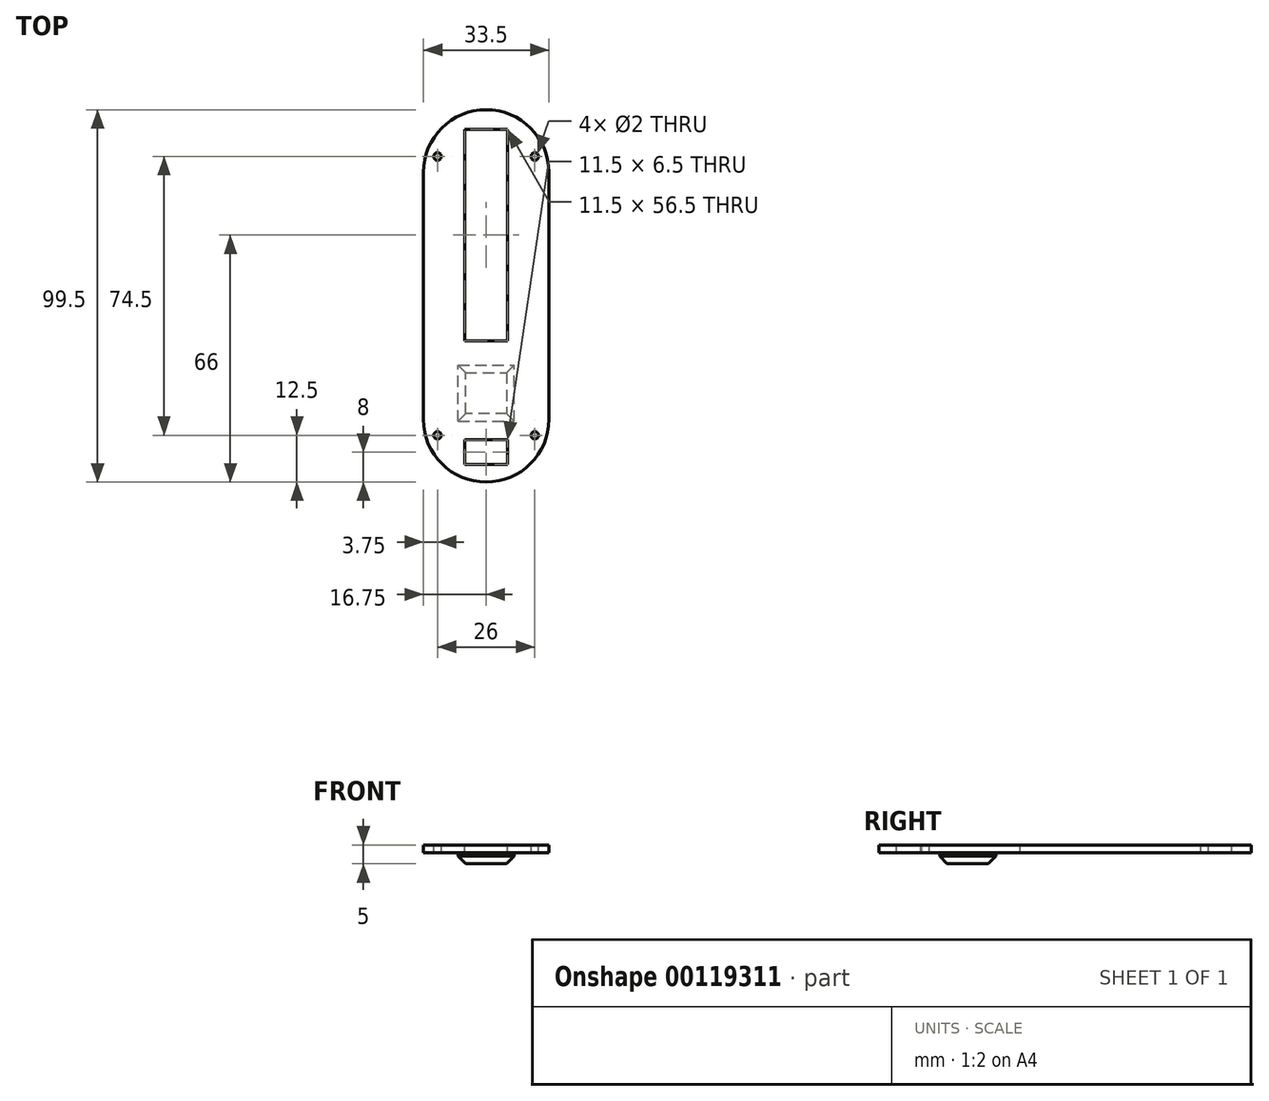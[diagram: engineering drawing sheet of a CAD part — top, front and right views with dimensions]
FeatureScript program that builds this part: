
annotation { "Feature Type Name" : "Feature", "Feature Type Description" : "" }
export const myFeature = defineFeature(function(context is Context, id is Id, definition is map)
    precondition{}
    {
        {
            var Q0;
            Q0=qCreatedBy(makeId("Top.planeOp"),FACE);
            var sketch = newSketch(context, id + "F0", { "sketchPlane" : qUnion([Q0])});
            skLineSegment(sketch, "E0", {"start": v(-96.93, -49.75) * mm, "end": v(93.91, -49.75) * mm, "construction": true});
            skLineSegment(sketch, "E1", {"start": v(-99.2, 49.75) * mm, "end": v(105.24, 49.75) * mm, "construction": true});
            skArc(sketch, "E2", {"start": v(16.75, 33) * mm, "mid": v(11.84, 44.84) * mm, "end": v(0, 49.75) * mm});
            skArc(sketch, "E3", {"start": v(0, -49.75) * mm, "mid": v(11.84, -44.84) * mm, "end": v(16.75, -33) * mm});
            skLineSegment(sketch, "E4.trimOffspring", {"start": v(16.75, 33) * mm, "end": v(16.75, -33) * mm});
            skArc(sketch, "E5.MirrorCS", {"start": v(-16.75, 33) * mm, "mid": v(-11.84, 44.84) * mm, "end": v(0, 49.75) * mm});
            skLineSegment(sketch, "E6.MirrorCS", {"start": v(-16.75, 33) * mm, "end": v(-16.75, -33) * mm});
            skArc(sketch, "E7.MirrorCS", {"start": v(0, -49.75) * mm, "mid": v(-11.84, -44.84) * mm, "end": v(-16.75, -33) * mm});
            skSolve(sketch);
        }
        {
            var Q0;
            Q0=qSketchRegion(id+"F0",true);
            extrude(context, id + "F1", {"entities" : qUnion([Q0]), "depth" : 2 * mm});
        }
        {
            var Q0;
            Q0=makeQuery(id+"F1.opExtrude","CAP_FACE",FACE,{"disambiguationData":[OSD([sQuery(id+"F0.wireOp",EDGE,"E2"),sQuery(id+"F0.wireOp",EDGE,"E3"),sQuery(id+"F0.wireOp",EDGE,"E4.trimOffspring"),sQuery(id+"F0.wireOp",EDGE,"E5.MirrorCS"),sQuery(id+"F0.wireOp",EDGE,"E6.MirrorCS"),sQuery(id+"F0.wireOp",EDGE,"E7.MirrorCS")])],"isStart":false});
            var sketch = newSketch(context, id + "F2", { "sketchPlane" : qUnion([Q0])});
            skLineSegment(sketch, "E8", {"start": v(-13, -67.26) * mm, "end": v(-13, 68.17) * mm, "construction": true});
            skLineSegment(sketch, "E9", {"start": v(13, -68.02) * mm, "end": v(13, 71.72) * mm, "construction": true});
            skLineSegment(sketch, "E10", {"start": v(-30.03, -49.75) * mm, "end": v(26.5, -49.75) * mm, "construction": true});
            skLineSegment(sketch, "E11", {"start": v(-29.95, -37.25) * mm, "end": v(27.55, -37.25) * mm, "construction": true});
            skLineSegment(sketch, "E12", {"start": v(-32.6, -19.75) * mm, "end": v(26.44, -19.75) * mm, "construction": true});
            skLineSegment(sketch, "E13", {"start": v(-30.61, 1.25) * mm, "end": v(28.66, 1.25) * mm, "construction": true});
            skCircle(sketch, "E14", {"center": v(-13, -37.25) * mm, "radius": 1 * mm});
            skCircle(sketch, "E15", {"center": v(13, -37.25) * mm, "radius": 1 * mm});
            skCircle(sketch, "E16.MirrorC", {"center": v(13, 37.25) * mm, "radius": 1 * mm});
            skCircle(sketch, "E17.MirrorC", {"center": v(-13, 37.25) * mm, "radius": 1 * mm});
            skSolve(sketch);
        }
        {
            var Q0;
            Q0=qSketchRegion(id+"F2",true);
            extrude(context, id + "F3", {"entities" : qUnion([Q0]), "operationType" : NewBodyOperationType.REMOVE, "endBound" : BoundingType.THROUGH_ALL, "oppositeDirection" : true, "depth" : 25 * mm});
        }
        {
            var Q0;
            Q0=makeQuery(id+"F1.opExtrude","CAP_FACE",FACE,{"disambiguationData":[OSD([sQuery(id+"F0.wireOp",EDGE,"E2"),sQuery(id+"F0.wireOp",EDGE,"E3"),sQuery(id+"F0.wireOp",EDGE,"E4.trimOffspring"),sQuery(id+"F0.wireOp",EDGE,"E5.MirrorCS"),sQuery(id+"F0.wireOp",EDGE,"E6.MirrorCS"),sQuery(id+"F0.wireOp",EDGE,"E7.MirrorCS")])],"isStart":false});
            var sketch = newSketch(context, id + "F4", { "sketchPlane" : qUnion([Q0])});
            skLineSegment(sketch, "E18", {"start": v(-31.43, 49.75) * mm, "end": v(26.37, 49.75) * mm, "construction": true});
            skLineSegment(sketch, "E19.0", {"start": v(-5.75, 44.5) * mm, "end": v(5.75, 44.5) * mm});
            skLineSegment(sketch, "E20.0", {"start": v(-5.75, -12) * mm, "end": v(5.75, -12) * mm});
            skLineSegment(sketch, "E21.0", {"start": v(-5.75, -38.5) * mm, "end": v(5.75, -38.5) * mm});
            skLineSegment(sketch, "E22.0", {"start": v(-5.75, -45) * mm, "end": v(5.75, -45) * mm});
            skLineSegment(sketch, "E23", {"start": v(5.75, 44.5) * mm, "end": v(5.75, -12) * mm});
            skLineSegment(sketch, "E24.MirrorCS", {"start": v(-5.75, 44.5) * mm, "end": v(-5.75, -12) * mm});
            skLineSegment(sketch, "E25.trimOffspring", {"start": v(5.75, -38.5) * mm, "end": v(5.75, -45) * mm});
            skLineSegment(sketch, "E26.trimOffspring", {"start": v(-5.75, -38.5) * mm, "end": v(-5.75, -45) * mm});
            skSolve(sketch);
        }
        {
            var Q0;
            Q0 = qSketchRegion(id + "F4", true);
            extrude(context, id + "F5", {"entities" : qUnion([Q0]), "operationType" : NewBodyOperationType.REMOVE, "endBound" : BoundingType.THROUGH_ALL, "oppositeDirection" : true, "depth" : 25 * mm});
        }
        {
            var Q0;
            Q0=makeQuery(id+"F1.opExtrude","CAP_FACE",FACE,{"disambiguationData":[OSD([sQuery(id+"F0.wireOp",EDGE,"E2"),sQuery(id+"F0.wireOp",EDGE,"E3"),sQuery(id+"F0.wireOp",EDGE,"E4.trimOffspring"),sQuery(id+"F0.wireOp",EDGE,"E5.MirrorCS"),sQuery(id+"F0.wireOp",EDGE,"E6.MirrorCS"),sQuery(id+"F0.wireOp",EDGE,"E7.MirrorCS")])],"isStart":true});
            var sketch = newSketch(context, id + "F6", { "sketchPlane" : qUnion([Q0])});
            skLineSegment(sketch, "E27.bottom", {"start": v(-7.5, 33.5) * mm, "end": v(7.5, 33.5) * mm});
            skLineSegment(sketch, "E27.top", {"start": v(-7.5, 18.5) * mm, "end": v(7.5, 18.5) * mm});
            skLineSegment(sketch, "E27.left", {"start": v(-7.5, 33.5) * mm, "end": v(-7.5, 18.5) * mm});
            skLineSegment(sketch, "E27.right", {"start": v(7.5, 33.5) * mm, "end": v(7.5, 18.5) * mm});
            skSolve(sketch);
        }
        {
            var Q0;
            Q0 = qSketchRegion(id + "F6", true);
            extrude(context, id + "F7", {"entities" : qUnion([Q0]), "operationType" : NewBodyOperationType.ADD, "depth" : 3 * mm, "offsetDistance" : 25 * mm});
        }
        {
            var Q0;
            Q0=makeQuery(id+"F7.opExtrude","CAP_EDGE",EDGE,{"disambiguationData":[OSD([sQuery(id+"F6.wireOp",EDGE,"E27.bottom")])],"isStart":false});
            var Q1;
            Q1=makeQuery(id+"F7.opExtrude","CAP_FACE",FACE,{"disambiguationData":[OSD([sQuery(id+"F6.wireOp",EDGE,"E27.bottom"),sQuery(id+"F6.wireOp",EDGE,"E27.top"),sQuery(id+"F6.wireOp",EDGE,"E27.left"),sQuery(id+"F6.wireOp",EDGE,"E27.right")])],"isStart":false});
            chamfer(context, id + "F8", {"entities" : qUnion([Q0, Q1]), "width" : 2 * mm, "tangentPropagation" : true});
        }
    });
